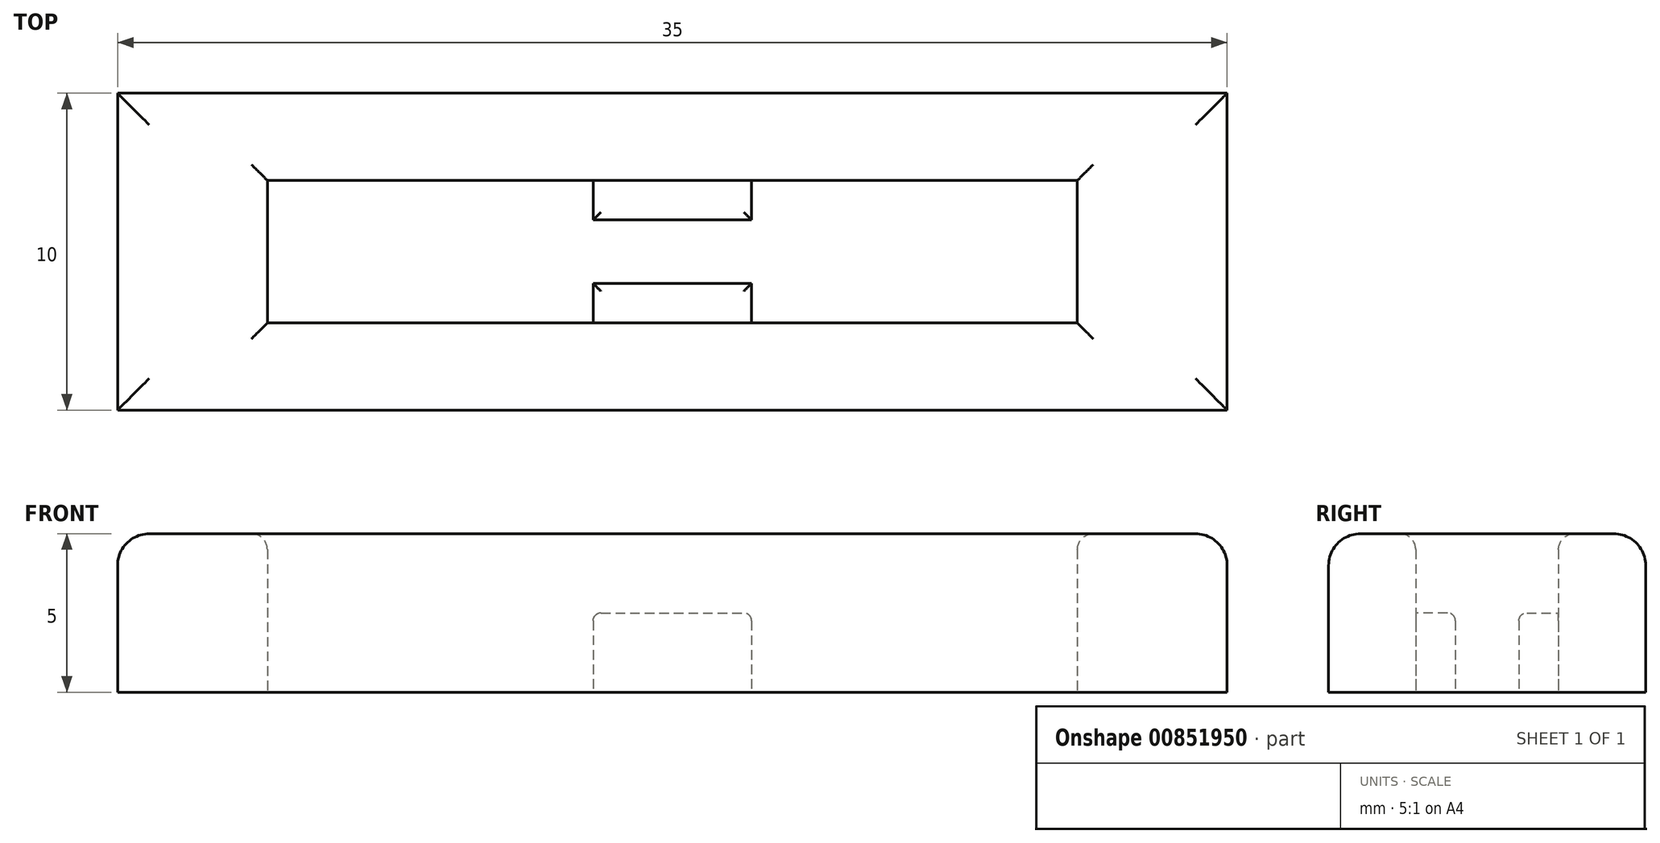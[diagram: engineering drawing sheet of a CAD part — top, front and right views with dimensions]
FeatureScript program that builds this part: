
annotation { "Feature Type Name" : "Feature", "Feature Type Description" : "" }
export const myFeature = defineFeature(function(context is Context, id is Id, definition is map)
    precondition{}
    {
        {
            var Q0;
            Q0=qCreatedBy(makeId("Top.planeOp"),FACE);
            var sketch = newSketch(context, id + "F0", { "sketchPlane" : qUnion([Q0])});
            skLineSegment(sketch, "E0.bottom", {"start": v(-17.5, 5) * mm, "end": v(17.5, 5) * mm});
            skLineSegment(sketch, "E0.top", {"start": v(-17.5, -5) * mm, "end": v(17.5, -5) * mm});
            skLineSegment(sketch, "E0.left", {"start": v(-17.5, 5) * mm, "end": v(-17.5, -5) * mm});
            skLineSegment(sketch, "E0.right", {"start": v(17.5, 5) * mm, "end": v(17.5, -5) * mm});
            skPoint(sketch, "E0.middle", {"position": v(0, 0) * mm});
            skLineSegment(sketch, "E1.bottom", {"start": v(-12.78, 2.25) * mm, "end": v(12.78, 2.25) * mm});
            skLineSegment(sketch, "E1.top", {"start": v(-12.78, -2.25) * mm, "end": v(12.78, -2.25) * mm});
            skLineSegment(sketch, "E1.left", {"start": v(-12.78, 2.25) * mm, "end": v(-12.78, -2.25) * mm});
            skLineSegment(sketch, "E1.right", {"start": v(12.78, 2.25) * mm, "end": v(12.78, -2.25) * mm});
            skLineSegment(sketch, "E2", {"start": v(-2.5, -1) * mm, "end": v(-2.5, -2.25) * mm});
            skLineSegment(sketch, "E3", {"start": v(2.5, -1) * mm, "end": v(2.5, -2.25) * mm});
            skLineSegment(sketch, "E4", {"start": v(2.5, 1) * mm, "end": v(2.5, 2.25) * mm});
            skLineSegment(sketch, "E5", {"start": v(-2.5, 1) * mm, "end": v(-2.5, 2.25) * mm});
            skLineSegment(sketch, "E6", {"start": v(2.5, -1) * mm, "end": v(-2.5, -1) * mm});
            skLineSegment(sketch, "E7", {"start": v(-2.5, 1) * mm, "end": v(2.5, 1) * mm});
            skSolve(sketch);
        }
        {
            var Q0;
            Q0=qCreatedBy(makeId("Top.planeOp"),FACE);
            cPlane(context, id + "F1", {"entities" : qUnion([Q0]), "cplaneType" : CPlaneType.OFFSET, "offset" : 0 * mm, "oppositeDirection" : true, "width" : 150 * mm, "height" : 150 * mm});
        }
        {
            var Q0;
            Q0 = qSketchRegion(id + "F0", true);
            extrude(context, id + "F2", {"entities" : qUnion([Q0]), "depth" : 5 * mm, "offsetDistance" : 25 * mm});
        }
        {
            var Q0;
            {var subQ0=sQuery(id+"F0.wireOp",EDGE,"E4");Q0=makeQuery(id+"F0.imprint","IMPRINT",FACE,{"disambiguationData":[TD([[makeQuery(id+"F0.imprint","IMPRINT",EDGE,{"derivedFrom":subQ0}),1.0]])]});}
            var Q1;
            {var subQ0=sQuery(id+"F0.wireOp",EDGE,"E2");Q1=makeQuery(id+"F0.imprint","IMPRINT",FACE,{"disambiguationData":[TD([[makeQuery(id+"F0.imprint","IMPRINT",EDGE,{"derivedFrom":subQ0}),1.0]])]});}
            extrude(context, id + "F3", {"entities" : qUnion([Q0, Q1]), "operationType" : NewBodyOperationType.ADD, "depth" : 2.5 * mm, "offsetDistance" : 25 * mm});
        }
        {
            var Q0;
            Q0=makeQuery(id+"F3.opExtrude","CAP_EDGE",EDGE,{"disambiguationData":[OSD([sQuery(id+"F0.wireOp",EDGE,"E4")])],"isStart":false});
            var Q1;
            Q1=makeQuery(id+"F3.opExtrude","CAP_EDGE",EDGE,{"disambiguationData":[OSD([sQuery(id+"F0.wireOp",EDGE,"E7")])],"isStart":false});
            var Q2;
            Q2=makeQuery(id+"F3.opExtrude","CAP_EDGE",EDGE,{"disambiguationData":[OSD([sQuery(id+"F0.wireOp",EDGE,"E5")])],"isStart":false});
            var Q3;
            Q3=makeQuery(id+"F3.opExtrude","CAP_EDGE",EDGE,{"disambiguationData":[OSD([sQuery(id+"F0.wireOp",EDGE,"E3")])],"isStart":false});
            var Q4;
            Q4=makeQuery(id+"F3.opExtrude","CAP_EDGE",EDGE,{"disambiguationData":[OSD([sQuery(id+"F0.wireOp",EDGE,"E2")])],"isStart":false});
            var Q5;
            Q5=makeQuery(id+"F3.opExtrude","CAP_EDGE",EDGE,{"disambiguationData":[OSD([sQuery(id+"F0.wireOp",EDGE,"E6")])],"isStart":false});
            fillet(context, id + "F4", {"entities" : qUnion([Q0, Q1, Q2, Q3, Q4, Q5]), "radius" : .25 * mm, "tangentPropagation" : true, "allowEdgeOverflow" : false});
        }
        {
            var Q0;
            Q0=makeQuery(id+"F2.opExtrude","CAP_EDGE",EDGE,{"disambiguationData":[OSD([sQuery(id+"F0.wireOp",EDGE,"E0.top")])],"isStart":false});
            var Q1;
            Q1=makeQuery(id+"F2.opExtrude","CAP_EDGE",EDGE,{"disambiguationData":[OSD([sQuery(id+"F0.wireOp",EDGE,"E0.bottom")])],"isStart":false});
            var Q2;
            Q2=makeQuery(id+"F2.opExtrude","CAP_EDGE",EDGE,{"disambiguationData":[OSD([sQuery(id+"F0.wireOp",EDGE,"E0.right")])],"isStart":false});
            var Q3;
            Q3=makeQuery(id+"F2.opExtrude","CAP_EDGE",EDGE,{"disambiguationData":[OSD([sQuery(id+"F0.wireOp",EDGE,"E0.left")])],"isStart":false});
            fillet(context, id + "F5", {"entities" : qUnion([Q0, Q1, Q2, Q3]), "radius" : 1 * mm, "tangentPropagation" : true, "allowEdgeOverflow" : false});
        }
        {
            var Q0;
            Q0=makeQuery(id+"F2.opExtrude","CAP_EDGE",EDGE,{"disambiguationData":[OSD([sQuery(id+"F0.wireOp",EDGE,"E1.bottom")])],"isStart":false});
            var Q1;
            Q1=makeQuery(id+"F2.opExtrude","CAP_EDGE",EDGE,{"disambiguationData":[OSD([sQuery(id+"F0.wireOp",EDGE,"E1.right")])],"isStart":false});
            var Q2;
            Q2=makeQuery(id+"F2.opExtrude","CAP_EDGE",EDGE,{"disambiguationData":[OSD([sQuery(id+"F0.wireOp",EDGE,"E1.top")])],"isStart":false});
            var Q3;
            Q3=makeQuery(id+"F2.opExtrude","CAP_EDGE",EDGE,{"disambiguationData":[OSD([sQuery(id+"F0.wireOp",EDGE,"E1.left")])],"isStart":false});
            fillet(context, id + "F6", {"entities" : qUnion([Q0, Q1, Q2, Q3]), "radius" : .5 * mm, "tangentPropagation" : true, "allowEdgeOverflow" : false});
        }
    });
